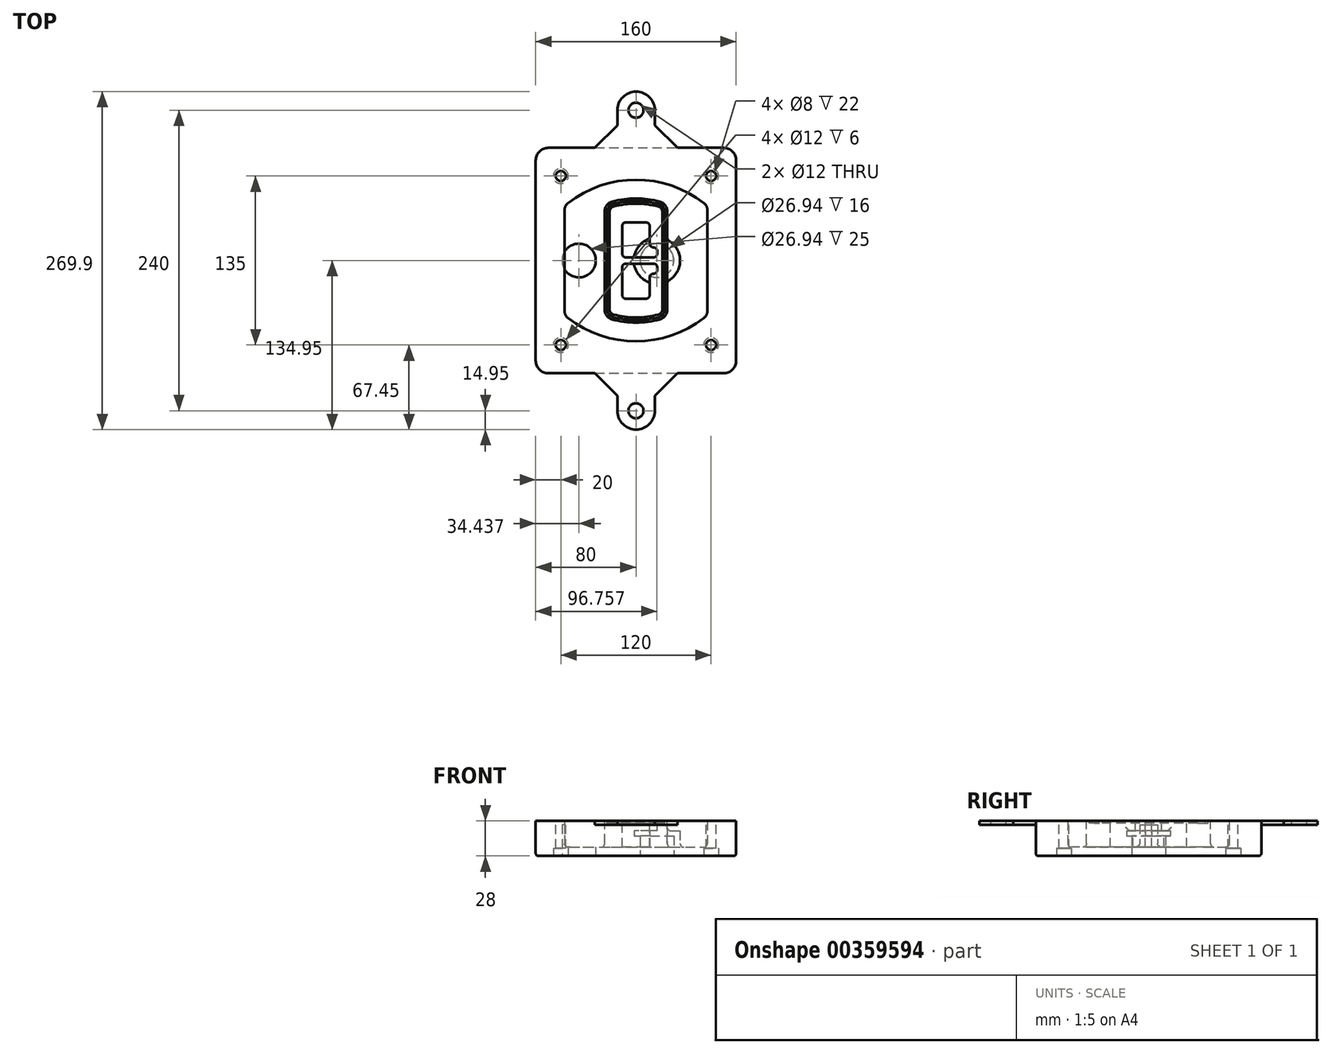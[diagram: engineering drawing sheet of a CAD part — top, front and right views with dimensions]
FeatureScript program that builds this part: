
annotation { "Feature Type Name" : "Feature", "Feature Type Description" : "" }
export const myFeature = defineFeature(function(context is Context, id is Id, definition is map)
    precondition{}
    {
        {
            var Q0;
            Q0=qCreatedBy(makeId("Top.planeOp"),FACE);
            var sketch = newSketch(context, id + "F0", { "sketchPlane" : qUnion([Q0])});
            skPoint(sketch, "E0.rect.middle", {"position": v(0, 0) * mm});
            skLineSegment(sketch, "E1.bottom", {"start": v(-70, -90) * mm, "end": v(70, -90) * mm});
            skLineSegment(sketch, "E1.top", {"start": v(-70, 90) * mm, "end": v(70, 90) * mm});
            skLineSegment(sketch, "E1.left", {"start": v(-80, -80) * mm, "end": v(-80, 80) * mm});
            skLineSegment(sketch, "E1.right", {"start": v(80, -80) * mm, "end": v(80, 80) * mm});
            skLineSegment(sketch, "E2", {"start": v(-80, 90) * mm, "end": v(80, -90) * mm, "construction": true});
            skLineSegment(sketch, "E3", {"start": v(80, 90) * mm, "end": v(-80, -90) * mm, "construction": true});
            skCircle(sketch, "E4", {"center": v(-60, 67.5) * mm, "radius": 4 * mm});
            skCircle(sketch, "E5", {"center": v(60, 67.5) * mm, "radius": 4 * mm});
            skCircle(sketch, "E6", {"center": v(60, -67.5) * mm, "radius": 4 * mm});
            skCircle(sketch, "E7", {"center": v(-60, -67.5) * mm, "radius": 4 * mm});
            skLineSegment(sketch, "E8", {"start": v(-60, 67.5) * mm, "end": v(60, 67.5) * mm, "construction": true});
            skLineSegment(sketch, "E9", {"start": v(60, 67.5) * mm, "end": v(60, -67.5) * mm, "construction": true});
            skLineSegment(sketch, "E10", {"start": v(60, -67.5) * mm, "end": v(-60, -67.5) * mm, "construction": true});
            skLineSegment(sketch, "E11", {"start": v(-60, -67.5) * mm, "end": v(-60, 67.5) * mm, "construction": true});
            skLineSegment(sketch, "E12", {"start": v(-60, 40.3) * mm, "end": v(-60, -40.3) * mm});
            skLineSegment(sketch, "E13", {"start": v(60, 40.3) * mm, "end": v(60, -40.3) * mm});
            skArc(sketch, "E14", {"start": v(56.15, 48.18) * mm, "mid": v(0, 67.5) * mm, "end": v(-56.15, 48.18) * mm});
            skArc(sketch, "E15", {"start": v(-56.15, -48.18) * mm, "mid": v(0, -67.5) * mm, "end": v(56.15, -48.18) * mm});
            skLineSegment(sketch, "E16", {"start": v(-60, 0) * mm, "end": v(60, 0) * mm, "construction": true});
            skPoint(sketch, "E17.visualSharp", {"position": v(-60, -45) * mm});
            skArc(sketch, "E17.filletArc", {"start": v(-60, -40.3) * mm, "mid": v(-58.99, -44.68) * mm, "end": v(-56.15, -48.18) * mm});
            skPoint(sketch, "E18.visualSharp", {"position": v(-60, 45) * mm});
            skArc(sketch, "E18.filletArc", {"start": v(-56.15, 48.18) * mm, "mid": v(-58.99, 44.68) * mm, "end": v(-60, 40.3) * mm});
            skPoint(sketch, "E19.visualSharp", {"position": v(60, 45) * mm});
            skArc(sketch, "E19.filletArc", {"start": v(60, 40.3) * mm, "mid": v(58.99, 44.68) * mm, "end": v(56.15, 48.18) * mm});
            skPoint(sketch, "E20.visualSharp", {"position": v(60, -45) * mm});
            skArc(sketch, "E20.filletArc", {"start": v(56.15, -48.18) * mm, "mid": v(58.99, -44.68) * mm, "end": v(60, -40.3) * mm});
            skPoint(sketch, "E21.visualSharp", {"position": v(-80, 90) * mm});
            skArc(sketch, "E21.filletArc", {"start": v(-70, 90) * mm, "mid": v(-77.07, 87.07) * mm, "end": v(-80, 80) * mm});
            skPoint(sketch, "E22.visualSharp", {"position": v(80, 90) * mm});
            skArc(sketch, "E22.filletArc", {"start": v(80, 80) * mm, "mid": v(77.07, 87.07) * mm, "end": v(70, 90) * mm});
            skPoint(sketch, "E23.visualSharp", {"position": v(80, -90) * mm});
            skArc(sketch, "E23.filletArc", {"start": v(70, -90) * mm, "mid": v(77.07, -87.07) * mm, "end": v(80, -80) * mm});
            skPoint(sketch, "E24.visualSharp", {"position": v(-80, -90) * mm});
            skArc(sketch, "E24.filletArc", {"start": v(-80, -80) * mm, "mid": v(-77.07, -87.07) * mm, "end": v(-70, -90) * mm});
            skArc(sketch, "E25.0", {"start": v(57, 40.3) * mm, "mid": v(56.3, 43.36) * mm, "end": v(54.3, 45.81) * mm});
            skLineSegment(sketch, "E25.1", {"start": v(57, 40.3) * mm, "end": v(57, -40.3) * mm});
            skArc(sketch, "E25.2", {"start": v(54.3, -45.81) * mm, "mid": v(56.3, -43.36) * mm, "end": v(57, -40.3) * mm});
            skArc(sketch, "E25.3", {"start": v(-54.3, -45.81) * mm, "mid": v(0, -64.5) * mm, "end": v(54.3, -45.81) * mm});
            skArc(sketch, "E25.4", {"start": v(-57, -40.3) * mm, "mid": v(-56.3, -43.36) * mm, "end": v(-54.3, -45.81) * mm});
            skArc(sketch, "E25.5", {"start": v(54.3, 45.81) * mm, "mid": v(0, 64.5) * mm, "end": v(-54.3, 45.81) * mm});
            skLineSegment(sketch, "E25.6", {"start": v(-57, 40.3) * mm, "end": v(-57, -40.3) * mm});
            skArc(sketch, "E25.7", {"start": v(-54.3, 45.81) * mm, "mid": v(-56.3, 43.36) * mm, "end": v(-57, 40.3) * mm});
            skArc(sketch, "E26.0", {"start": v(-58.62, 51.33) * mm, "mid": v(-62.58, 46.43) * mm, "end": v(-64, 40.3) * mm});
            skArc(sketch, "E26.1", {"start": v(58.62, 51.33) * mm, "mid": v(0, 71.5) * mm, "end": v(-58.62, 51.33) * mm});
            skArc(sketch, "E26.2", {"start": v(64, 40.3) * mm, "mid": v(62.58, 46.43) * mm, "end": v(58.62, 51.33) * mm});
            skLineSegment(sketch, "E26.3", {"start": v(64, 40.3) * mm, "end": v(64, -40.3) * mm});
            skArc(sketch, "E26.4", {"start": v(58.62, -51.33) * mm, "mid": v(62.58, -46.43) * mm, "end": v(64, -40.3) * mm});
            skLineSegment(sketch, "E26.5", {"start": v(-64, 40.3) * mm, "end": v(-64, -40.3) * mm});
            skArc(sketch, "E26.6", {"start": v(-58.62, -51.33) * mm, "mid": v(0, -71.5) * mm, "end": v(58.62, -51.33) * mm});
            skArc(sketch, "E26.7", {"start": v(-64, -40.3) * mm, "mid": v(-62.58, -46.43) * mm, "end": v(-58.62, -51.33) * mm});
            skSolve(sketch);
        }
        {
            var Q0;
            Q0=makeQuery(id+"F0.imprint","IMPRINT",FACE,{"disambiguationData":[TD([[makeQuery(id+"F0.imprint","IMPRINT",EDGE,{"derivedFrom":sQuery(id+"F0.wireOp",EDGE,"E1.bottom")}),1.0]])]});
            var Q1;
            Q1=makeQuery(id+"F0.imprint","IMPRINT",FACE,{"disambiguationData":[TD([[makeQuery(id+"F0.imprint","IMPRINT",EDGE,{"derivedFrom":sQuery(id+"F0.wireOp",EDGE,"E12")}),1.0]])]});
            var Q2;
            Q2=makeQuery(id+"F0.imprint","IMPRINT",FACE,{"disambiguationData":[TD([[makeQuery(id+"F0.imprint","IMPRINT",EDGE,{"derivedFrom":sQuery(id+"F0.wireOp",EDGE,"E25.0")}),1.0]])]});
            var Q3;
            Q3=makeQuery(id+"F0.imprint","IMPRINT",FACE,{"disambiguationData":[TD([[makeQuery(id+"F0.imprint","IMPRINT",EDGE,{"derivedFrom":sQuery(id+"F0.wireOp",EDGE,"E12")}),-1.0]])]});
            extrude(context, id + "F1", {"entities" : qUnion([Q0, Q1, Q2, Q3]), "oppositeDirection" : true, "depth" : 25 * mm});
        }
        {
            var Q0;
            Q0=makeQuery(id+"F0.imprint","IMPRINT",FACE,{"disambiguationData":[TD([[makeQuery(id+"F0.imprint","IMPRINT",EDGE,{"derivedFrom":sQuery(id+"F0.wireOp",EDGE,"E12")}),1.0]])]});
            extrude(context, id + "F2", {"entities" : qUnion([Q0]), "operationType" : NewBodyOperationType.ADD, "depth" : 3 * mm});
        }
        {
            var Q0;
            Q0=makeQuery(id+"F0.imprint","IMPRINT",FACE,{"disambiguationData":[TD([[makeQuery(id+"F0.imprint","IMPRINT",EDGE,{"derivedFrom":sQuery(id+"F0.wireOp",EDGE,"E25.0")}),1.0]])]});
            extrude(context, id + "F3", {"entities" : qUnion([Q0]), "operationType" : NewBodyOperationType.REMOVE, "oppositeDirection" : true, "depth" : 18 * mm});
        }
        {
            var Q0;
            Q0=makeQuery(id+"F2.opExtrude","CAP_FACE",FACE,{"disambiguationData":[OSD([sQuery(id+"F0.wireOp",EDGE,"E12"),sQuery(id+"F0.wireOp",EDGE,"E13"),sQuery(id+"F0.wireOp",EDGE,"E14"),sQuery(id+"F0.wireOp",EDGE,"E15"),sQuery(id+"F0.wireOp",EDGE,"E17.filletArc"),sQuery(id+"F0.wireOp",EDGE,"E18.filletArc"),sQuery(id+"F0.wireOp",EDGE,"E19.filletArc"),sQuery(id+"F0.wireOp",EDGE,"E20.filletArc"),sQuery(id+"F0.wireOp",EDGE,"E25.0"),sQuery(id+"F0.wireOp",EDGE,"E25.1"),sQuery(id+"F0.wireOp",EDGE,"E25.2"),sQuery(id+"F0.wireOp",EDGE,"E25.3"),sQuery(id+"F0.wireOp",EDGE,"E25.4"),sQuery(id+"F0.wireOp",EDGE,"E25.5"),sQuery(id+"F0.wireOp",EDGE,"E25.6"),sQuery(id+"F0.wireOp",EDGE,"E25.7")])],"isStart":false});
            var sketch = newSketch(context, id + "F4", { "sketchPlane" : qUnion([Q0])});
            skArc(sketch, "E27.0", {"start": v(-19.08, -46.97) * mm, "mid": v(0, -49.5) * mm, "end": v(19.08, -46.97) * mm});
            skArc(sketch, "E28.0", {"start": v(19.08, 46.97) * mm, "mid": v(0, 49.5) * mm, "end": v(-19.08, 46.97) * mm});
            skLineSegment(sketch, "E29", {"start": v(-25, 39.25) * mm, "end": v(-25, -39.25) * mm});
            skLineSegment(sketch, "E30", {"start": v(25, 39.25) * mm, "end": v(25, -39.25) * mm});
            skLineSegment(sketch, "E31", {"start": v(-25, 45.1) * mm, "end": v(25, 45.1) * mm, "construction": true});
            skLineSegment(sketch, "E32", {"start": v(-25, -45.1) * mm, "end": v(25, -45.1) * mm, "construction": true});
            skPoint(sketch, "E33.visualSharp", {"position": v(-25, 45.1) * mm});
            skArc(sketch, "E33.filletArc", {"start": v(-19.08, 46.97) * mm, "mid": v(-23.35, 44.11) * mm, "end": v(-25, 39.25) * mm});
            skPoint(sketch, "E34.visualSharp", {"position": v(25, 45.1) * mm});
            skArc(sketch, "E34.filletArc", {"start": v(25, 39.25) * mm, "mid": v(23.35, 44.11) * mm, "end": v(19.08, 46.97) * mm});
            skPoint(sketch, "E35.visualSharp", {"position": v(25, -45.1) * mm});
            skArc(sketch, "E35.filletArc", {"start": v(19.08, -46.97) * mm, "mid": v(23.35, -44.11) * mm, "end": v(25, -39.25) * mm});
            skPoint(sketch, "E36.visualSharp", {"position": v(-25, -45.1) * mm});
            skArc(sketch, "E36.filletArc", {"start": v(-25, -39.25) * mm, "mid": v(-23.35, -44.11) * mm, "end": v(-19.08, -46.97) * mm});
            skArc(sketch, "E37.0", {"start": v(54.3, 45.81) * mm, "mid": v(0, 64.5) * mm, "end": v(-54.3, 45.81) * mm});
            skArc(sketch, "E37.1", {"start": v(-54.3, 45.81) * mm, "mid": v(-56.3, 43.36) * mm, "end": v(-57, 40.3) * mm});
            skLineSegment(sketch, "E37.2", {"start": v(-57, 40.3) * mm, "end": v(-57, -40.3) * mm});
            skArc(sketch, "E37.3", {"start": v(-57, -40.3) * mm, "mid": v(-56.3, -43.36) * mm, "end": v(-54.3, -45.81) * mm});
            skArc(sketch, "E37.4", {"start": v(-54.3, -45.81) * mm, "mid": v(0, -64.5) * mm, "end": v(54.3, -45.81) * mm});
            skArc(sketch, "E37.5", {"start": v(54.3, -45.81) * mm, "mid": v(56.3, -43.36) * mm, "end": v(57, -40.3) * mm});
            skLineSegment(sketch, "E37.6", {"start": v(57, 40.3) * mm, "end": v(57, -40.3) * mm});
            skArc(sketch, "E37.7", {"start": v(57, 40.3) * mm, "mid": v(56.3, 43.36) * mm, "end": v(54.3, 45.81) * mm});
            skLineSegment(sketch, "E38.0", {"start": v(23, 39.25) * mm, "end": v(23, -39.25) * mm});
            skArc(sketch, "E38.1", {"start": v(18.56, -45.04) * mm, "mid": v(21.76, -42.9) * mm, "end": v(23, -39.25) * mm});
            skArc(sketch, "E38.2", {"start": v(-18.56, -45.04) * mm, "mid": v(0, -47.5) * mm, "end": v(18.56, -45.04) * mm});
            skArc(sketch, "E38.3", {"start": v(-23, -39.25) * mm, "mid": v(-21.76, -42.9) * mm, "end": v(-18.56, -45.04) * mm});
            skLineSegment(sketch, "E38.4", {"start": v(-23, 39.25) * mm, "end": v(-23, -39.25) * mm});
            skArc(sketch, "E38.5", {"start": v(23, 39.25) * mm, "mid": v(21.76, 42.9) * mm, "end": v(18.56, 45.04) * mm});
            skArc(sketch, "E38.6", {"start": v(-18.56, 45.04) * mm, "mid": v(-21.76, 42.9) * mm, "end": v(-23, 39.25) * mm});
            skArc(sketch, "E38.7", {"start": v(18.56, 45.04) * mm, "mid": v(0, 47.5) * mm, "end": v(-18.56, 45.04) * mm});
            skArc(sketch, "E39.0", {"start": v(21, 39.25) * mm, "mid": v(20.18, 41.68) * mm, "end": v(18.04, 43.1) * mm});
            skLineSegment(sketch, "E39.1", {"start": v(21, 39.25) * mm, "end": v(21, -39.25) * mm});
            skArc(sketch, "E39.2", {"start": v(18.04, -43.1) * mm, "mid": v(20.18, -41.68) * mm, "end": v(21, -39.25) * mm});
            skArc(sketch, "E39.3", {"start": v(-18.04, -43.1) * mm, "mid": v(0, -45.5) * mm, "end": v(18.04, -43.1) * mm});
            skArc(sketch, "E39.4", {"start": v(-21, -39.25) * mm, "mid": v(-20.18, -41.68) * mm, "end": v(-18.04, -43.1) * mm});
            skArc(sketch, "E39.5", {"start": v(18.04, 43.1) * mm, "mid": v(0, 45.5) * mm, "end": v(-18.04, 43.1) * mm});
            skLineSegment(sketch, "E39.6", {"start": v(-21, 39.25) * mm, "end": v(-21, -39.25) * mm});
            skArc(sketch, "E39.7", {"start": v(-18.04, 43.1) * mm, "mid": v(-20.18, 41.68) * mm, "end": v(-21, 39.25) * mm});
            skLineSegment(sketch, "E40", {"start": v(-25, 0) * mm, "end": v(25, 0) * mm, "construction": true});
            skLineSegment(sketch, "E41", {"start": v(-11, 5.5) * mm, "end": v(-11, 27.5) * mm});
            skLineSegment(sketch, "E42", {"start": v(-8, 30.5) * mm, "end": v(8, 30.5) * mm});
            skLineSegment(sketch, "E43", {"start": v(11, 27.5) * mm, "end": v(11, 13.5) * mm});
            skLineSegment(sketch, "E44", {"start": v(14, 10.5) * mm, "end": v(14, 10.5) * mm});
            skLineSegment(sketch, "E45", {"start": v(17, 7.5) * mm, "end": v(17, 5.5) * mm});
            skLineSegment(sketch, "E46", {"start": v(14, 2.5) * mm, "end": v(-8, 2.5) * mm});
            skPoint(sketch, "E47.visualSharp", {"position": v(-11, 30.5) * mm});
            skArc(sketch, "E47.filletArc", {"start": v(-8, 30.5) * mm, "mid": v(-10.12, 29.62) * mm, "end": v(-11, 27.5) * mm});
            skPoint(sketch, "E48.visualSharp", {"position": v(11, 30.5) * mm});
            skArc(sketch, "E48.filletArc", {"start": v(11, 27.5) * mm, "mid": v(10.12, 29.62) * mm, "end": v(8, 30.5) * mm});
            skPoint(sketch, "E49.visualSharp", {"position": v(11, 10.5) * mm});
            skArc(sketch, "E49.filletArc", {"start": v(11, 13.5) * mm, "mid": v(11.88, 11.38) * mm, "end": v(14, 10.5) * mm});
            skPoint(sketch, "E50.visualSharp", {"position": v(17, 10.5) * mm});
            skArc(sketch, "E50.filletArc", {"start": v(17, 7.5) * mm, "mid": v(16.12, 9.62) * mm, "end": v(14, 10.5) * mm});
            skPoint(sketch, "E51.visualSharp", {"position": v(17, 2.5) * mm});
            skArc(sketch, "E51.filletArc", {"start": v(14, 2.5) * mm, "mid": v(16.12, 3.38) * mm, "end": v(17, 5.5) * mm});
            skPoint(sketch, "E52.visualSharp", {"position": v(-11, 2.5) * mm});
            skArc(sketch, "E52.filletArc", {"start": v(-11, 5.5) * mm, "mid": v(-10.12, 3.38) * mm, "end": v(-8, 2.5) * mm});
            skLineSegment(sketch, "E53.0.MirrorCS", {"start": v(14, -2.5) * mm, "end": v(-8, -2.5) * mm});
            skArc(sketch, "E54.0.MirrorCS", {"start": v(-11, -5.5) * mm, "mid": v(-10.12, -3.38) * mm, "end": v(-8, -2.5) * mm});
            skLineSegment(sketch, "E55.0.MirrorCS", {"start": v(-11, -5.5) * mm, "end": v(-11, -27.5) * mm});
            skArc(sketch, "E56.0.MirrorCS", {"start": v(-8, -30.5) * mm, "mid": v(-10.12, -29.62) * mm, "end": v(-11, -27.5) * mm});
            skLineSegment(sketch, "E57.0.MirrorCS", {"start": v(-8, -30.5) * mm, "end": v(8, -30.5) * mm});
            skArc(sketch, "E58.0.MirrorCS", {"start": v(11, -27.5) * mm, "mid": v(10.12, -29.62) * mm, "end": v(8, -30.5) * mm});
            skLineSegment(sketch, "E59.0.MirrorCS", {"start": v(11, -27.5) * mm, "end": v(11, -13.5) * mm});
            skArc(sketch, "E60.0.MirrorCS", {"start": v(11, -13.5) * mm, "mid": v(11.88, -11.38) * mm, "end": v(14, -10.5) * mm});
            skArc(sketch, "E61.0.MirrorCS", {"start": v(17, -7.5) * mm, "mid": v(16.12, -9.62) * mm, "end": v(14, -10.5) * mm});
            skLineSegment(sketch, "E62.0.MirrorCS", {"start": v(17, -7.5) * mm, "end": v(17, -5.5) * mm});
            skArc(sketch, "E63.0.MirrorCS", {"start": v(14, -2.5) * mm, "mid": v(16.12, -3.38) * mm, "end": v(17, -5.5) * mm});
            skSolve(sketch);
        }
        {
            var Q0;
            Q0=makeQuery(id+"F4.imprint","IMPRINT",FACE,{"disambiguationData":[TD([[makeQuery(id+"F4.imprint","IMPRINT",EDGE,{"derivedFrom":sQuery(id+"F4.wireOp",EDGE,"E27.0")}),1.0]])]});
            var Q1;
            Q1=makeQuery(id+"F4.imprint","IMPRINT",FACE,{"disambiguationData":[TD([[makeQuery(id+"F4.imprint","IMPRINT",EDGE,{"derivedFrom":sQuery(id+"F4.wireOp",EDGE,"E38.0")}),-1.0]])]});
            var Q2;
            Q2=makeQuery(id+"F4.imprint","IMPRINT",FACE,{"disambiguationData":[TD([[makeQuery(id+"F4.imprint","IMPRINT",EDGE,{"derivedFrom":sQuery(id+"F4.wireOp",EDGE,"E39.0")}),1.0]])]});
            extrude(context, id + "F5", {"entities" : qUnion([Q0, Q1, Q2]), "operationType" : NewBodyOperationType.ADD, "endBound" : BoundingType.UP_TO_NEXT, "oppositeDirection" : true, "depth" : 25 * mm});
        }
        {
            var Q0;
            Q0=makeQuery(id+"F4.imprint","IMPRINT",FACE,{"disambiguationData":[TD([[makeQuery(id+"F4.imprint","IMPRINT",EDGE,{"derivedFrom":sQuery(id+"F4.wireOp",EDGE,"E38.0")}),-1.0]])]});
            extrude(context, id + "F6", {"entities" : qUnion([Q0]), "operationType" : NewBodyOperationType.REMOVE, "oppositeDirection" : true, "depth" : 2 * mm});
        }
        {
            var Q0;
            Q0=makeQuery(id+"F1.opExtrude","CAP_FACE",FACE,{"disambiguationData":[OSD([sQuery(id+"F0.wireOp",EDGE,"E1.bottom"),sQuery(id+"F0.wireOp",EDGE,"E1.top"),sQuery(id+"F0.wireOp",EDGE,"E1.left"),sQuery(id+"F0.wireOp",EDGE,"E1.right"),sQuery(id+"F0.wireOp",EDGE,"E4"),sQuery(id+"F0.wireOp",EDGE,"E5"),sQuery(id+"F0.wireOp",EDGE,"E6"),sQuery(id+"F0.wireOp",EDGE,"E7"),sQuery(id+"F0.wireOp",EDGE,"E21.filletArc"),sQuery(id+"F0.wireOp",EDGE,"E22.filletArc"),sQuery(id+"F0.wireOp",EDGE,"E23.filletArc"),sQuery(id+"F0.wireOp",EDGE,"E24.filletArc")])],"isStart":false});
            var sketch = newSketch(context, id + "F7", { "sketchPlane" : qUnion([Q0])});
            skCircle(sketch, "E64", {"center": v(16.76, 0) * mm, "radius": 13.47 * mm});
            skCircle(sketch, "E65", {"center": v(-45.56, 0) * mm, "radius": 13.47 * mm});
            skLineSegment(sketch, "E66", {"start": v(80, 0) * mm, "end": v(-80, 0) * mm});
            skCircle(sketch, "E67", {"center": v(16.76, 0) * mm, "radius": 18.47 * mm});
            skCircle(sketch, "E68", {"center": v(60, -67.5) * mm, "radius": 6 * mm});
            skCircle(sketch, "E69", {"center": v(-60, -67.5) * mm, "radius": 6 * mm});
            skCircle(sketch, "E70", {"center": v(-60, 67.5) * mm, "radius": 6 * mm});
            skCircle(sketch, "E71", {"center": v(60, 67.5) * mm, "radius": 6 * mm});
            skSolve(sketch);
        }
        {
            var Q0;
            {var subQ1=sQuery(id+"F7.wireOp",EDGE,"E66");var subQ4=sQuery(id+"F7.wireOp",EDGE,"E64");var subQ6=makeQuery(id+"F7.imprint","INTERSECT",VERTEX,{"disambiguationData":[OD(0.0)],"derivedFrom":[subQ4,subQ1]});Q0=makeQuery(id+"F7.imprint","IMPRINT",FACE,{"disambiguationData":[TD([[makeQuery(id+"F7.imprint","IMPRINT",EDGE,{"disambiguationData":[TD([[subQ6,-1.0]])],"derivedFrom":subQ4}),-1.0]])]});}
            var Q1;
            {var subQ0=sQuery(id+"F7.wireOp",EDGE,"E66");var subQ1=sQuery(id+"F7.wireOp",EDGE,"E64");var subQ3=makeQuery(id+"F7.imprint","INTERSECT",VERTEX,{"disambiguationData":[OD(0.0)],"derivedFrom":[subQ1,subQ0]});Q1=makeQuery(id+"F7.imprint","IMPRINT",FACE,{"disambiguationData":[TD([[makeQuery(id+"F7.imprint","IMPRINT",EDGE,{"disambiguationData":[TD([[subQ3,-1.0]])],"derivedFrom":subQ1}),1.0]])]});}
            var Q2;
            {var subQ0=sQuery(id+"F7.wireOp",EDGE,"E66");var subQ1=sQuery(id+"F7.wireOp",EDGE,"E64");var subQ3=makeQuery(id+"F7.imprint","INTERSECT",VERTEX,{"disambiguationData":[OD(0.0)],"derivedFrom":[subQ1,subQ0]});Q2=makeQuery(id+"F7.imprint","IMPRINT",FACE,{"disambiguationData":[TD([[makeQuery(id+"F7.imprint","IMPRINT",EDGE,{"disambiguationData":[TD([[subQ3,1.0]])],"derivedFrom":subQ1}),1.0]])]});}
            var Q3;
            {var subQ1=sQuery(id+"F7.wireOp",EDGE,"E66");var subQ4=sQuery(id+"F7.wireOp",EDGE,"E64");var subQ6=makeQuery(id+"F7.imprint","INTERSECT",VERTEX,{"disambiguationData":[OD(0.0)],"derivedFrom":[subQ4,subQ1]});Q3=makeQuery(id+"F7.imprint","IMPRINT",FACE,{"disambiguationData":[TD([[makeQuery(id+"F7.imprint","IMPRINT",EDGE,{"disambiguationData":[TD([[subQ6,1.0]])],"derivedFrom":subQ4}),-1.0]])]});}
            extrude(context, id + "F8", {"entities" : qUnion([Q0, Q1, Q2, Q3]), "operationType" : NewBodyOperationType.ADD, "oppositeDirection" : true, "depth" : 20 * mm});
        }
        {
            var Q0;
            {var subQ0=sQuery(id+"F7.wireOp",EDGE,"E66");var subQ1=sQuery(id+"F7.wireOp",EDGE,"E64");var subQ3=makeQuery(id+"F7.imprint","INTERSECT",VERTEX,{"disambiguationData":[OD(0.0)],"derivedFrom":[subQ1,subQ0]});Q0=makeQuery(id+"F7.imprint","IMPRINT",FACE,{"disambiguationData":[TD([[makeQuery(id+"F7.imprint","IMPRINT",EDGE,{"disambiguationData":[TD([[subQ3,-1.0]])],"derivedFrom":subQ1}),1.0]])]});}
            var Q1;
            {var subQ0=sQuery(id+"F7.wireOp",EDGE,"E66");var subQ1=sQuery(id+"F7.wireOp",EDGE,"E64");var subQ3=makeQuery(id+"F7.imprint","INTERSECT",VERTEX,{"disambiguationData":[OD(0.0)],"derivedFrom":[subQ1,subQ0]});Q1=makeQuery(id+"F7.imprint","IMPRINT",FACE,{"disambiguationData":[TD([[makeQuery(id+"F7.imprint","IMPRINT",EDGE,{"disambiguationData":[TD([[subQ3,1.0]])],"derivedFrom":subQ1}),1.0]])]});}
            extrude(context, id + "F9", {"entities" : qUnion([Q0, Q1]), "operationType" : NewBodyOperationType.REMOVE, "oppositeDirection" : true, "depth" : 16 * mm});
        }
        {
            var Q0;
            {var subQ0=sQuery(id+"F7.wireOp",EDGE,"E66");var subQ1=sQuery(id+"F7.wireOp",EDGE,"E65");var subQ3=makeQuery(id+"F7.imprint","INTERSECT",VERTEX,{"disambiguationData":[OD(0.0)],"derivedFrom":[subQ1,subQ0]});Q0=makeQuery(id+"F7.imprint","IMPRINT",FACE,{"disambiguationData":[TD([[makeQuery(id+"F7.imprint","IMPRINT",EDGE,{"disambiguationData":[TD([[subQ3,-1.0]])],"derivedFrom":subQ1}),1.0]])]});}
            var Q1;
            {var subQ0=sQuery(id+"F7.wireOp",EDGE,"E66");var subQ1=sQuery(id+"F7.wireOp",EDGE,"E65");var subQ3=makeQuery(id+"F7.imprint","INTERSECT",VERTEX,{"disambiguationData":[OD(0.0)],"derivedFrom":[subQ1,subQ0]});Q1=makeQuery(id+"F7.imprint","IMPRINT",FACE,{"disambiguationData":[TD([[makeQuery(id+"F7.imprint","IMPRINT",EDGE,{"disambiguationData":[TD([[subQ3,1.0]])],"derivedFrom":subQ1}),1.0]])]});}
            extrude(context, id + "F10", {"entities" : qUnion([Q0, Q1]), "operationType" : NewBodyOperationType.REMOVE, "oppositeDirection" : true, "depth" : 25 * mm});
        }
        {
            var Q0;
            Q0=makeQuery(id+"F7.imprint","IMPRINT",FACE,{"disambiguationData":[TD([[makeQuery(id+"F7.imprint","IMPRINT",EDGE,{"derivedFrom":sQuery(id+"F7.wireOp",EDGE,"E68")}),1.0]])]});
            var Q1;
            Q1=makeQuery(id+"F7.imprint","IMPRINT",FACE,{"disambiguationData":[TD([[makeQuery(id+"F7.imprint","IMPRINT",EDGE,{"derivedFrom":makeQuery(id+"F1.opExtrude","CAP_EDGE",EDGE,{"disambiguationData":[OSD([sQuery(id+"F0.wireOp",EDGE,"E5")])],"isStart":false})}),-1.0]])]});
            var Q2;
            Q2=makeQuery(id+"F7.imprint","IMPRINT",FACE,{"disambiguationData":[TD([[makeQuery(id+"F7.imprint","IMPRINT",EDGE,{"derivedFrom":sQuery(id+"F7.wireOp",EDGE,"E69")}),1.0]])]});
            var Q3;
            Q3=makeQuery(id+"F7.imprint","IMPRINT",FACE,{"disambiguationData":[TD([[makeQuery(id+"F7.imprint","IMPRINT",EDGE,{"derivedFrom":makeQuery(id+"F1.opExtrude","CAP_EDGE",EDGE,{"disambiguationData":[OSD([sQuery(id+"F0.wireOp",EDGE,"E4")])],"isStart":false})}),-1.0]])]});
            var Q4;
            Q4=makeQuery(id+"F7.imprint","IMPRINT",FACE,{"disambiguationData":[TD([[makeQuery(id+"F7.imprint","IMPRINT",EDGE,{"derivedFrom":sQuery(id+"F7.wireOp",EDGE,"E70")}),1.0]])]});
            var Q5;
            Q5=makeQuery(id+"F7.imprint","IMPRINT",FACE,{"disambiguationData":[TD([[makeQuery(id+"F7.imprint","IMPRINT",EDGE,{"derivedFrom":makeQuery(id+"F1.opExtrude","CAP_EDGE",EDGE,{"disambiguationData":[OSD([sQuery(id+"F0.wireOp",EDGE,"E7")])],"isStart":false})}),-1.0]])]});
            var Q6;
            Q6=makeQuery(id+"F7.imprint","IMPRINT",FACE,{"disambiguationData":[TD([[makeQuery(id+"F7.imprint","IMPRINT",EDGE,{"derivedFrom":sQuery(id+"F7.wireOp",EDGE,"E71")}),1.0]])]});
            var Q7;
            Q7=makeQuery(id+"F7.imprint","IMPRINT",FACE,{"disambiguationData":[TD([[makeQuery(id+"F7.imprint","IMPRINT",EDGE,{"derivedFrom":makeQuery(id+"F1.opExtrude","CAP_EDGE",EDGE,{"disambiguationData":[OSD([sQuery(id+"F0.wireOp",EDGE,"E6")])],"isStart":false})}),-1.0]])]});
            extrude(context, id + "F11", {"entities" : qUnion([Q0, Q1, Q2, Q3, Q4, Q5, Q6, Q7]), "operationType" : NewBodyOperationType.REMOVE, "oppositeDirection" : true, "depth" : 6 * mm});
        }
        {
            var Q0;
            Q0=makeQuery(id+"F9.boolean.opBoolean","COPY",FACE,{"derivedFrom":makeQuery(id+"F9.opExtrude","CAP_FACE",FACE,{"disambiguationData":[OSD([sQuery(id+"F7.wireOp",EDGE,"E64")])],"isStart":false})});
            var sketch = newSketch(context, id + "F12", { "sketchPlane" : qUnion([Q0])});
            skArc(sketch, "E72.0", {"start": v(11, 17.55) * mm, "mid": v(2.57, 11.82) * mm, "end": v(-1.54, 2.5) * mm});
            skArc(sketch, "E72.1", {"start": v(-1.54, -2.5) * mm, "mid": v(2.57, -11.82) * mm, "end": v(11, -17.55) * mm});
            skLineSegment(sketch, "E73", {"start": v(-1.54, -2.5) * mm, "end": v(14, -2.5) * mm});
            skLineSegment(sketch, "E74.0", {"start": v(14, 2.5) * mm, "end": v(-1.54, 2.5) * mm});
            skArc(sketch, "E74.1", {"start": v(14, 2.5) * mm, "mid": v(16.12, 3.38) * mm, "end": v(17, 5.5) * mm});
            skLineSegment(sketch, "E74.2", {"start": v(17, 7.5) * mm, "end": v(17, 5.5) * mm});
            skArc(sketch, "E74.3", {"start": v(17, 7.5) * mm, "mid": v(16.12, 9.62) * mm, "end": v(14, 10.5) * mm});
            skArc(sketch, "E74.4", {"start": v(11, 13.5) * mm, "mid": v(11.88, 11.38) * mm, "end": v(14, 10.5) * mm});
            skLineSegment(sketch, "E74.5", {"start": v(11, 17.55) * mm, "end": v(11, 13.5) * mm});
            skLineSegment(sketch, "E74.7", {"start": v(14, -2.5) * mm, "end": v(-1.54, -2.5) * mm});
            skArc(sketch, "E74.8", {"start": v(14, -2.5) * mm, "mid": v(16.12, -3.38) * mm, "end": v(17, -5.5) * mm});
            skLineSegment(sketch, "E74.9", {"start": v(17, -7.5) * mm, "end": v(17, -5.5) * mm});
            skArc(sketch, "E74.10", {"start": v(17, -7.5) * mm, "mid": v(16.12, -9.62) * mm, "end": v(14, -10.5) * mm});
            skArc(sketch, "E74.11", {"start": v(11, -13.5) * mm, "mid": v(11.88, -11.38) * mm, "end": v(14, -10.5) * mm});
            skLineSegment(sketch, "E74.12", {"start": v(11, -17.55) * mm, "end": v(11, -13.5) * mm});
            skPoint(sketch, "E75.orphan", {"position": v(11, -27.5) * mm});
            skPoint(sketch, "E76.orphan", {"position": v(-8, -2.5) * mm});
            skPoint(sketch, "E77.orphan", {"position": v(-8, 2.5) * mm});
            skPoint(sketch, "E78.orphan", {"position": v(11, 27.5) * mm});
            skSolve(sketch);
        }
        {
            var Q0;
            {var subQ7=sQuery(id+"F12.wireOp",EDGE,"E72.0");var subQ14=sQuery(id+"F12.wireOp",EDGE,"E72.1");var subQ16=sQuery(id+"F12.wireOp",EDGE,"E74.1");var subQ18=sQuery(id+"F12.wireOp",EDGE,"E74.8");Q0=qUnion([makeQuery(id+"F12.imprint","IMPRINT",FACE,{"disambiguationData":[TD([[makeQuery(id+"F12.imprint","IMPRINT",EDGE,{"derivedFrom":subQ7}),1.0]])]}),makeQuery(id+"F12.imprint","IMPRINT",FACE,{"disambiguationData":[TD([[makeQuery(id+"F12.imprint","IMPRINT",EDGE,{"derivedFrom":subQ14}),1.0]])]}),makeQuery(id+"F12.imprint","IMPRINT",FACE,{"disambiguationData":[TD([[makeQuery(id+"F12.imprint","IMPRINT",EDGE,{"derivedFrom":subQ16}),1.0]])]}),makeQuery(id+"F12.imprint","IMPRINT",FACE,{"disambiguationData":[TD([[makeQuery(id+"F12.imprint","IMPRINT",EDGE,{"derivedFrom":subQ18}),-1.0]])]})]);}
            var Q1;
            Q1=makeQuery(id+"F5.boolean.opBoolean","SPLIT",FACE,{"disambiguationData":[TD([makeQuery(id+"F5.opExtrude","SWEPT_FACE",FACE,{"disambiguationData":[OSD([sQuery(id+"F4.wireOp",EDGE,"E41")])]})])],"derivedFrom":makeQuery(id+"F3.boolean.opBoolean","COPY",FACE,{"derivedFrom":makeQuery(id+"F3.opExtrude","CAP_FACE",FACE,{"disambiguationData":[OSD([sQuery(id+"F0.wireOp",EDGE,"E25.0"),sQuery(id+"F0.wireOp",EDGE,"E25.1"),sQuery(id+"F0.wireOp",EDGE,"E25.2"),sQuery(id+"F0.wireOp",EDGE,"E25.3"),sQuery(id+"F0.wireOp",EDGE,"E25.4"),sQuery(id+"F0.wireOp",EDGE,"E25.5"),sQuery(id+"F0.wireOp",EDGE,"E25.6"),sQuery(id+"F0.wireOp",EDGE,"E25.7")])],"isStart":false})})});
            extrude(context, id + "F13", {"entities" : qUnion([Q0]), "operationType" : NewBodyOperationType.REMOVE, "endBound" : BoundingType.UP_TO_SURFACE, "endBoundEntityFace" : qUnion([Q1]), "depth" : 25 * mm});
        }
        {
            var Q0;
            Q0=makeQuery(id+"F3.boolean.opBoolean","COPY",EDGE,{"derivedFrom":makeQuery(id+"F3.opExtrude","CAP_EDGE",EDGE,{"disambiguationData":[OSD([sQuery(id+"F0.wireOp",EDGE,"E25.6")])],"isStart":false})});
            var Q1;
            Q1=makeQuery(id+"F8.boolean.opBoolean","INTERSECT",EDGE,{"derivedFrom":[makeQuery(id+"F5.opExtrude","SWEPT_FACE",FACE,{"disambiguationData":[OSD([sQuery(id+"F4.wireOp",EDGE,"E30")])]}),makeQuery(id+"F8.opExtrude","CAP_FACE",FACE,{"disambiguationData":[OSD([sQuery(id+"F7.wireOp",EDGE,"E67")])],"isStart":false})]});
            var Q2;
            Q2=makeQuery(id+"F8.boolean.opBoolean","INTERSECT",EDGE,{"disambiguationData":[OD(1.0)],"derivedFrom":[makeQuery(id+"F5.opExtrude","SWEPT_FACE",FACE,{"disambiguationData":[OSD([sQuery(id+"F4.wireOp",EDGE,"E30")])]}),makeQuery(id+"F8.opExtrude","SWEPT_FACE",FACE,{"disambiguationData":[OSD([sQuery(id+"F7.wireOp",EDGE,"E67")])]})]});
            var Q3;
            {var subQ0=sQuery(id+"F4.wireOp",EDGE,"E30");Q3=makeQuery(id+"F8.boolean.opBoolean","SPLIT",EDGE,{"disambiguationData":[TD([makeQuery(id+"F5.opExtrude","SWEPT_FACE",FACE,{"disambiguationData":[OSD([sQuery(id+"F4.wireOp",EDGE,"E35.filletArc")])]})])],"derivedFrom":makeQuery(id+"F5.opExtrude","CAP_EDGE",EDGE,{"disambiguationData":[OSD([subQ0])],"isStart":false})});}
            var Q4;
            {var subQ0=sQuery(id+"F0.wireOp",EDGE,"E25.7");var subQ1=sQuery(id+"F0.wireOp",EDGE,"E25.1");var subQ2=sQuery(id+"F0.wireOp",EDGE,"E25.6");var subQ3=sQuery(id+"F0.wireOp",EDGE,"E25.5");var subQ4=sQuery(id+"F0.wireOp",EDGE,"E25.4");var subQ5=sQuery(id+"F0.wireOp",EDGE,"E25.0");var subQ6=sQuery(id+"F0.wireOp",EDGE,"E25.2");var subQ7=sQuery(id+"F0.wireOp",EDGE,"E25.3");Q4=makeQuery(id+"F8.boolean.opBoolean","INTERSECT",EDGE,{"derivedFrom":[makeQuery(id+"F5.boolean.opBoolean","SPLIT",FACE,{"disambiguationData":[TD([makeQuery(id+"F2.opExtrude","SWEPT_FACE",FACE,{"disambiguationData":[OSD([subQ5])]})])],"derivedFrom":makeQuery(id+"F3.boolean.opBoolean","COPY",FACE,{"derivedFrom":makeQuery(id+"F3.opExtrude","CAP_FACE",FACE,{"disambiguationData":[OSD([subQ5,subQ1,subQ6,subQ7,subQ4,subQ3,subQ2,subQ0])],"isStart":false})})}),makeQuery(id+"F8.opExtrude","SWEPT_FACE",FACE,{"disambiguationData":[OSD([sQuery(id+"F7.wireOp",EDGE,"E67")])]})]});}
            var Q5;
            Q5=makeQuery(id+"F8.boolean.opBoolean","INTERSECT",EDGE,{"disambiguationData":[OD(0.0)],"derivedFrom":[makeQuery(id+"F5.opExtrude","SWEPT_FACE",FACE,{"disambiguationData":[OSD([sQuery(id+"F4.wireOp",EDGE,"E30")])]}),makeQuery(id+"F8.opExtrude","SWEPT_FACE",FACE,{"disambiguationData":[OSD([sQuery(id+"F7.wireOp",EDGE,"E67")])]})]});
            fillet(context, id + "F14", {"entities" : qUnion([Q0, Q1, Q2, Q3, Q4, Q5]), "radius" : 3 * mm, "tangentPropagation" : true, "allowEdgeOverflow" : false});
        }
        {
            var Q0;
            Q0=makeQuery(id+"F1.opExtrude","CAP_EDGE",EDGE,{"disambiguationData":[OSD([sQuery(id+"F0.wireOp",EDGE,"E1.bottom")])],"isStart":false});
            fillet(context, id + "F15", {"entities" : qUnion([Q0]), "radius" : 2 * mm, "tangentPropagation" : true, "allowEdgeOverflow" : false});
        }
        {
            var Q0;
            {var subQ0=sQuery(id+"F0.wireOp",EDGE,"E21.filletArc");var subQ1=sQuery(id+"F0.wireOp",EDGE,"E7");var subQ2=sQuery(id+"F0.wireOp",EDGE,"E6");var subQ3=sQuery(id+"F0.wireOp",EDGE,"E5");var subQ4=sQuery(id+"F0.wireOp",EDGE,"E4");var subQ5=sQuery(id+"F0.wireOp",EDGE,"E22.filletArc");var subQ6=sQuery(id+"F0.wireOp",EDGE,"E1.bottom");var subQ7=sQuery(id+"F0.wireOp",EDGE,"E1.right");var subQ8=sQuery(id+"F0.wireOp",EDGE,"E1.top");var subQ9=sQuery(id+"F0.wireOp",EDGE,"E1.left");var subQ10=sQuery(id+"F0.wireOp",EDGE,"E23.filletArc");var subQ11=sQuery(id+"F0.wireOp",EDGE,"E24.filletArc");Q0=makeQuery(id+"F2.boolean.opBoolean","SPLIT",FACE,{"disambiguationData":[TD([makeQuery(id+"F1.opExtrude","SWEPT_FACE",FACE,{"disambiguationData":[OSD([subQ6])]})])],"derivedFrom":makeQuery(id+"F1.opExtrude","CAP_FACE",FACE,{"disambiguationData":[OSD([subQ6,subQ8,subQ9,subQ7,subQ4,subQ3,subQ2,subQ1,subQ0,subQ5,subQ10,subQ11])],"isStart":true})});}
            var sketch = newSketch(context, id + "F16", { "sketchPlane" : qUnion([Q0])});
            skLineSegment(sketch, "E79", {"start": v(0, 90) * mm, "end": v(0, 120) * mm, "construction": true});
            skCircle(sketch, "E80", {"center": v(0, 120) * mm, "radius": 6 * mm});
            skArc(sketch, "E81", {"start": v(15.14, 120) * mm, "mid": v(0.14, 134.95) * mm, "end": v(-14.86, 120) * mm});
            skLineSegment(sketch, "E82", {"start": v(-14.86, 120) * mm, "end": v(-14.86, 108) * mm});
            skLineSegment(sketch, "E83", {"start": v(15.14, 120) * mm, "end": v(15.17, 108) * mm});
            skLineSegment(sketch, "E84", {"start": v(15.17, 108) * mm, "end": v(33.17, 90) * mm});
            skLineSegment(sketch, "E85", {"start": v(-14.86, 108) * mm, "end": v(-32.86, 90) * mm});
            skLineSegment(sketch, "E86", {"start": v(80, 0) * mm, "end": v(-80, 0) * mm, "construction": true});
            skLineSegment(sketch, "E87.MirrorCS", {"start": v(-14.86, -108) * mm, "end": v(-32.86, -90) * mm});
            skLineSegment(sketch, "E88.MirrorCS", {"start": v(-14.86, -120) * mm, "end": v(-14.86, -108) * mm});
            skArc(sketch, "E89.MirrorCS", {"start": v(15.14, -120) * mm, "mid": v(0.14, -134.95) * mm, "end": v(-14.86, -120) * mm});
            skLineSegment(sketch, "E90.MirrorCS", {"start": v(15.14, -120) * mm, "end": v(15.17, -108) * mm});
            skLineSegment(sketch, "E91.MirrorCS", {"start": v(15.17, -108) * mm, "end": v(33.17, -90) * mm});
            skCircle(sketch, "E92.MirrorC", {"center": v(0, -120) * mm, "radius": 6 * mm});
            skLineSegment(sketch, "E93.MirrorCS", {"start": v(0, -90) * mm, "end": v(0, -120) * mm, "construction": true});
            skSolve(sketch);
        }
        {
            var Q0;
            Q0=makeQuery(id+"F16.imprint","IMPRINT",FACE,{"disambiguationData":[TD([[makeQuery(id+"F16.imprint","IMPRINT",EDGE,{"derivedFrom":makeQuery(id+"F1.opExtrude","CAP_EDGE",EDGE,{"disambiguationData":[OSD([sQuery(id+"F0.wireOp",EDGE,"E1.left")])],"isStart":true})}),-1.0]])]});
            var Q1;
            Q1=makeQuery(id+"F16.imprint","IMPRINT",FACE,{"disambiguationData":[TD([[makeQuery(id+"F16.imprint","IMPRINT",EDGE,{"derivedFrom":sQuery(id+"F16.wireOp",EDGE,"E80")}),-1.0]])]});
            var Q2;
            {var subQ0=sQuery(id+"F16.wireOp",EDGE,"E87.MirrorCS");Q2=makeQuery(id+"F16.imprint","IMPRINT",FACE,{"disambiguationData":[TD([[makeQuery(id+"F16.imprint","IMPRINT",EDGE,{"derivedFrom":subQ0}),-1.0]])]});}
            var Q3;
            Q3=makeQuery(id+"F2.opExtrude","CAP_FACE",FACE,{"disambiguationData":[OSD([sQuery(id+"F0.wireOp",EDGE,"E12"),sQuery(id+"F0.wireOp",EDGE,"E13"),sQuery(id+"F0.wireOp",EDGE,"E14"),sQuery(id+"F0.wireOp",EDGE,"E15"),sQuery(id+"F0.wireOp",EDGE,"E17.filletArc"),sQuery(id+"F0.wireOp",EDGE,"E18.filletArc"),sQuery(id+"F0.wireOp",EDGE,"E19.filletArc"),sQuery(id+"F0.wireOp",EDGE,"E20.filletArc"),sQuery(id+"F0.wireOp",EDGE,"E25.0"),sQuery(id+"F0.wireOp",EDGE,"E25.1"),sQuery(id+"F0.wireOp",EDGE,"E25.2"),sQuery(id+"F0.wireOp",EDGE,"E25.3"),sQuery(id+"F0.wireOp",EDGE,"E25.4"),sQuery(id+"F0.wireOp",EDGE,"E25.5"),sQuery(id+"F0.wireOp",EDGE,"E25.6"),sQuery(id+"F0.wireOp",EDGE,"E25.7")])],"isStart":false});
            extrude(context, id + "F17", {"entities" : qUnion([Q0, Q1, Q2]), "operationType" : NewBodyOperationType.ADD, "endBound" : BoundingType.UP_TO_SURFACE, "endBoundEntityFace" : qUnion([Q3]), "depth" : 25 * mm});
        }
    });
